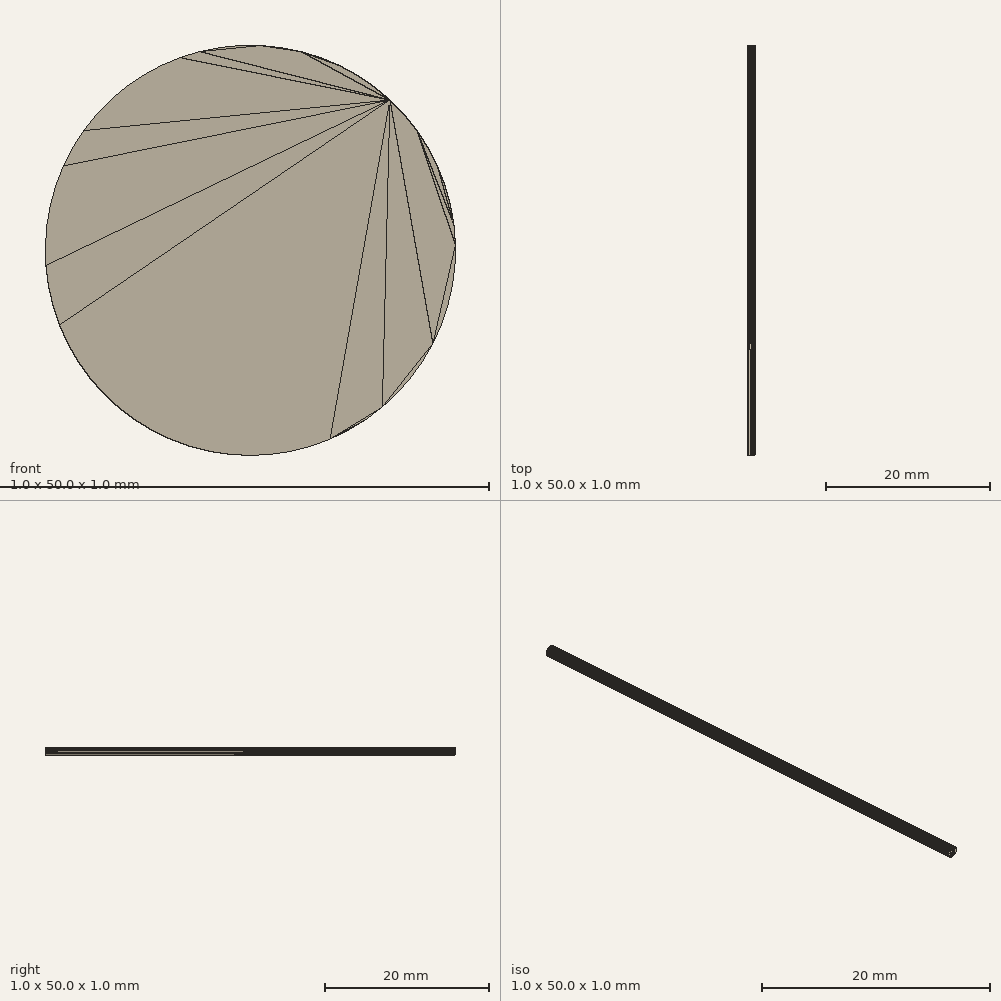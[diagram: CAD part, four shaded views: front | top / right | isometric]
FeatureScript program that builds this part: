
annotation { "Feature Type Name" : "Feature", "Feature Type Description" : "" }
export const myFeature = defineFeature(function(context is Context, id is Id, definition is map)
    precondition{}
    {
        {
            var Q0;
            Q0=qCreatedBy(makeId("Front.planeOp"),FACE);
            var sketch = newSketch(context, id + "F0", { "sketchPlane" : qUnion([Q0])});
            skCircle(sketch, "E0", {"center": v(-65.26, 48.42) * mm, "radius": 0.5 * mm});
            skSolve(sketch);
        }
        {
            var Q0;
            Q0=makeQuery(id+"F0.imprint","IMPRINT",FACE,{"disambiguationData":[TD([[makeQuery(id+"F0.imprint","IMPRINT",EDGE,{"derivedFrom":sQuery(id+"F0.wireOp",EDGE,"E0")}),1.0]])]});
            extrude(context, id + "F1", {"entities" : qUnion([Q0]), "depth" : 50 * mm, "offsetDistance" : 25 * mm});
        }
    });
